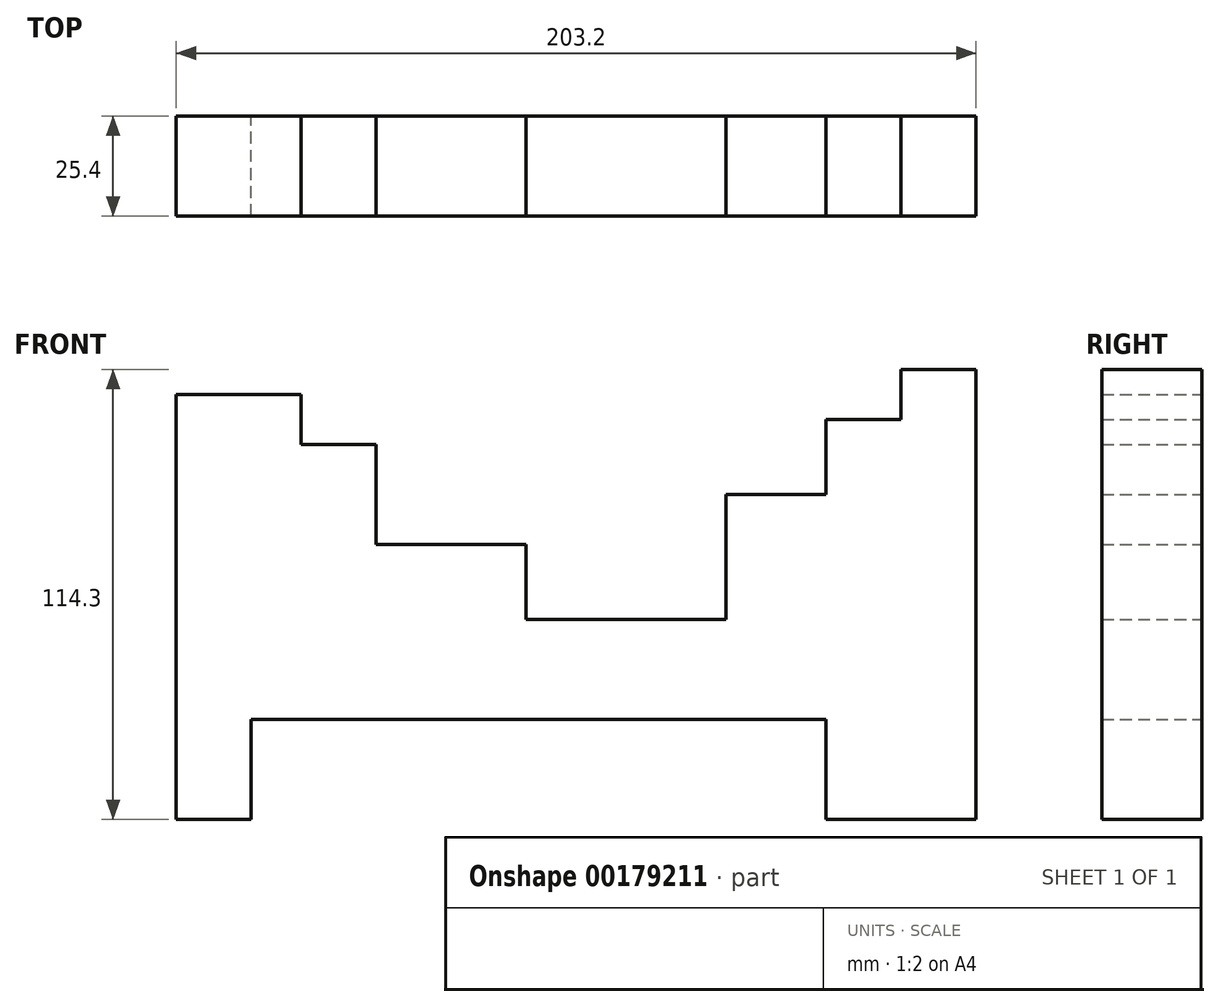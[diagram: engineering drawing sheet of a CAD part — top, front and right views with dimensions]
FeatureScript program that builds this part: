
annotation { "Feature Type Name" : "Feature", "Feature Type Description" : "" }
export const myFeature = defineFeature(function(context is Context, id is Id, definition is map)
    precondition{}
    {
        {
            var Q0;
            Q0=qCreatedBy(makeId("Front.planeOp"),FACE);
            var sketch = newSketch(context, id + "F0", { "sketchPlane" : qUnion([Q0])});
            skLineSegment(sketch, "E0", {"start": v(0, 0) * mm, "end": v(19.05, 0) * mm});
            skLineSegment(sketch, "E1", {"start": v(19.05, 0) * mm, "end": v(19.05, 25.4) * mm});
            skLineSegment(sketch, "E2", {"start": v(19.05, 25.4) * mm, "end": v(165.1, 25.4) * mm});
            skLineSegment(sketch, "E3", {"start": v(165.1, 25.4) * mm, "end": v(165.1, 0) * mm});
            skLineSegment(sketch, "E4", {"start": v(165.1, 0) * mm, "end": v(203.2, 0) * mm});
            skLineSegment(sketch, "E5", {"start": v(203.2, 0) * mm, "end": v(203.2, 114.3) * mm});
            skLineSegment(sketch, "E6", {"start": v(203.2, 114.3) * mm, "end": v(184.15, 114.3) * mm});
            skLineSegment(sketch, "E7", {"start": v(184.15, 114.3) * mm, "end": v(184.15, 101.6) * mm});
            skLineSegment(sketch, "E8", {"start": v(184.15, 101.6) * mm, "end": v(165.1, 101.6) * mm});
            skLineSegment(sketch, "E9", {"start": v(165.1, 101.6) * mm, "end": v(165.1, 82.55) * mm});
            skLineSegment(sketch, "E10", {"start": v(165.1, 82.55) * mm, "end": v(139.7, 82.55) * mm});
            skLineSegment(sketch, "E11", {"start": v(139.7, 82.55) * mm, "end": v(139.7, 50.8) * mm});
            skLineSegment(sketch, "E12", {"start": v(139.7, 50.8) * mm, "end": v(88.9, 50.8) * mm});
            skLineSegment(sketch, "E13", {"start": v(88.9, 50.8) * mm, "end": v(88.9, 69.85) * mm});
            skLineSegment(sketch, "E14", {"start": v(88.9, 69.85) * mm, "end": v(50.8, 69.85) * mm});
            skLineSegment(sketch, "E15", {"start": v(50.8, 69.85) * mm, "end": v(50.8, 95.25) * mm});
            skLineSegment(sketch, "E16", {"start": v(50.8, 95.25) * mm, "end": v(31.75, 95.25) * mm});
            skLineSegment(sketch, "E17", {"start": v(31.75, 95.25) * mm, "end": v(31.75, 107.95) * mm});
            skLineSegment(sketch, "E18", {"start": v(0, 0) * mm, "end": v(0, 107.95) * mm});
            skLineSegment(sketch, "E19", {"start": v(0, 107.95) * mm, "end": v(31.75, 107.95) * mm});
            skSolve(sketch);
        }
        {
            var Q0;
            Q0 = qSketchRegion(id + "F0", true);
            extrude(context, id + "F1", {"entities" : qUnion([Q0]), "depth" : 25.4 * mm});
        }
    });
